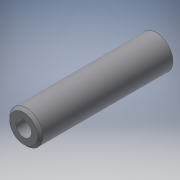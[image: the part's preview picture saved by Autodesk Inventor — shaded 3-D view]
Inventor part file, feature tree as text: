
AUTODESK INVENTOR PART (.ipt)
format: ipt  version: 2016 (Build 200138000, 138)  size: 97,792 bytes
history: native  units: mm
features: extrude x1, chamfer x1, sketch x1
ambient origin geometry x8: Origin, YZ Plane, XZ Plane, XY Plane, X Axis, Y Axis, Z Axis, Center Point
bodies: Solid1 (feature_tree)
feature tree (3):
  extrude  "Extrusion1"  Depth=2.0mm
  chamfer  "Chamfer1"  Distance=200.0mm
  sketch  "Sketch1"  dims[d0=50.0mm d1=23.5mm d2=200.0mm d3=0.0mm d4=4.0mm d5=2.0mm d6=45.0deg]
